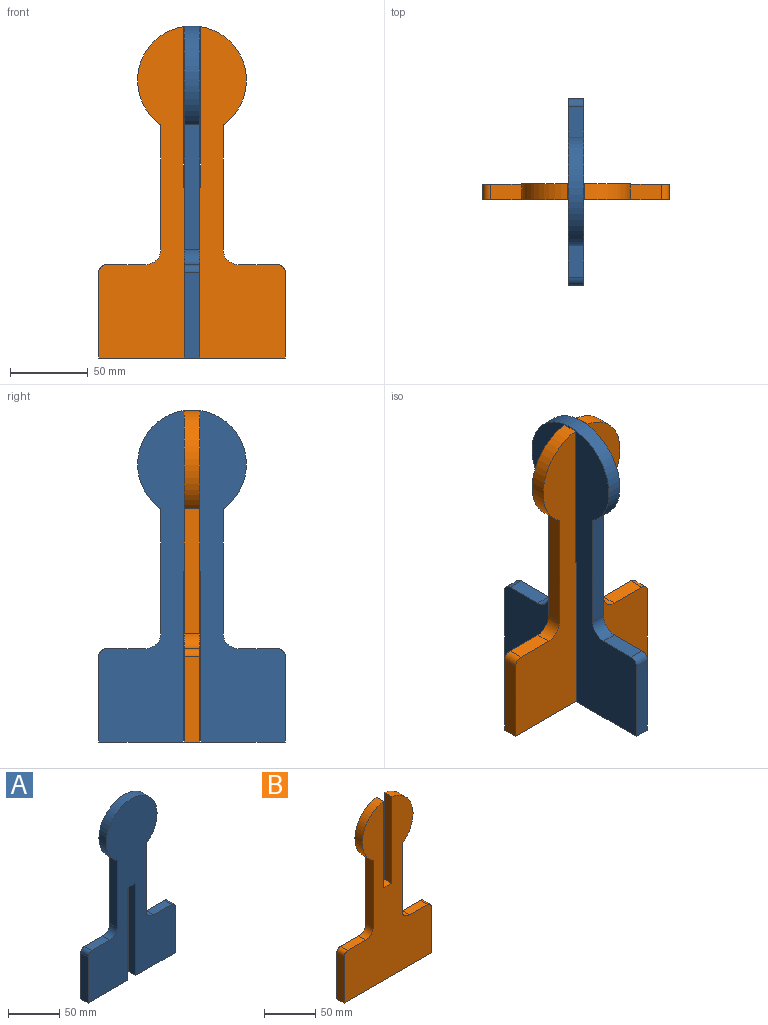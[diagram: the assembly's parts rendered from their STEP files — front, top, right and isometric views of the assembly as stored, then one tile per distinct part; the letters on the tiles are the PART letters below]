
ASSEMBLY  parts=2 mates=1
PART A: 18 faces, bbox 120x10x213.7 mm
  f0: plane 80x10mm, normal (1,0,0), area 800mm2, adj f1,f15,f16,f17
  f1: cylinder r=35mm len=70mm, axis (0,1,0), area 1773.3mm2, adj f0,f2,f16,f17
  f2: plane 80x10mm, normal (-1,0,0), area 800mm2, adj f1,f3,f16,f17
  f3: cylinder r=10mm len=10mm, axis (0,1,0), area 157.1mm2, adj f2,f4,f16,f17
  f4: plane 25x10mm, normal (0,0,1), area 250mm2, adj f3,f5,f16,f17
  f5: cylinder r=5mm len=10mm, axis (0,1,0), area 78.5mm2, adj f4,f6,f16,f17
  f6: plane 55x10mm, normal (-1,0,0), area 550mm2, adj f5,f7,f16,f17
  f7: plane 54.5x10mm, normal (0,0,-1), area 545mm2, adj f6,f8,f16,f17
  f8: plane 110x10mm, normal (1,0,0), area 1100mm2, adj f7,f9,f16,f17
  f9: plane 11x10mm, normal (0,0,-1), area 110mm2, adj f8,f10,f16,f17
  f10: plane 110x10mm, normal (-1,0,0), area 1100mm2, adj f9,f11,f16,f17
  f11: plane 54.5x10mm, normal (0,0,-1), area 545mm2, adj f10,f12,f16,f17
  f12: plane 55x10mm, normal (1,0,0), area 550mm2, adj f11,f13,f16,f17
  f13: cylinder r=5mm len=10mm, axis (0,1,0), area 78.5mm2, adj f12,f14,f16,f17
  f14: plane 25x10mm, normal (0,0,1), area 250mm2, adj f13,f15,f16,f17
  f15: cylinder r=10mm len=10mm, axis (0,1,0), area 157.1mm2, adj f0,f14,f16,f17
  f16: plane 213.72x120mm, normal (0,-1,0), area 13300mm2, adj f0,f1,f2,f3,f4,f5,f6,f7
  f17: plane 213.72x120mm, normal (0,1,0), area 13300mm2, adj f0,f1,f2,f3,f4,f5,f6,f7
PART B: 18 faces, bbox 120x10x213.3 mm
  f0: plane 103.29x10mm, normal (1,0,0), area 1032.9mm2, adj f1,f15,f16,f17
  f1: cylinder r=35mm len=63.29mm, axis (0,-1,0), area 831.4mm2, adj f0,f2,f16,f17
  f2: plane 80x10mm, normal (-1,0,0), area 800mm2, adj f1,f3,f16,f17
  f3: cylinder r=10mm len=10mm, axis (0,-1,0), area 157.1mm2, adj f2,f4,f16,f17
  f4: plane 25x10mm, normal (0,0,1), area 250mm2, adj f3,f5,f16,f17
  f5: cylinder r=5mm len=10mm, axis (0,-1,0), area 78.5mm2, adj f4,f6,f16,f17
  f6: plane 55x10mm, normal (-1,0,0), area 550mm2, adj f5,f7,f16,f17
  f7: plane 120x10mm, normal (0,0,-1), area 1200mm2, adj f6,f8,f16,f17
  f8: plane 55x10mm, normal (1,0,0), area 550mm2, adj f7,f9,f16,f17
  f9: cylinder r=5mm len=10mm, axis (0,-1,0), area 78.5mm2, adj f8,f10,f16,f17
  f10: plane 25x10mm, normal (0,0,1), area 250mm2, adj f9,f11,f16,f17
  f11: cylinder r=10mm len=10mm, axis (0,-1,0), area 157.1mm2, adj f10,f12,f16,f17
  f12: plane 80x10mm, normal (1,0,0), area 800mm2, adj f11,f13,f16,f17
  f13: cylinder r=35mm len=63.29mm, axis (0,-1,0), area 831.4mm2, adj f12,f14,f16,f17
  f14: plane 103.29x10mm, normal (-1,0,0), area 1032.9mm2, adj f13,f15,f16,f17
  f15: plane 11x10mm, normal (0,0,1), area 110mm2, adj f0,f14,f16,f17
  f16: plane 213.29x120mm, normal (0,1,0), area 13370.6mm2, adj f0,f1,f2,f3,f4,f5,f6,f7
  f17: plane 213.29x120mm, normal (0,-1,0), area 13370.6mm2, adj f0,f1,f2,f3,f4,f5,f6,f7
PLACE A rot(axis=(0,0,1),90deg) t=(-5,5,0)mm
PLACE B at identity
MATE fastened A.f9 <-> B.f15  axis (0,0,-1) through (0,5,42.88)mm
